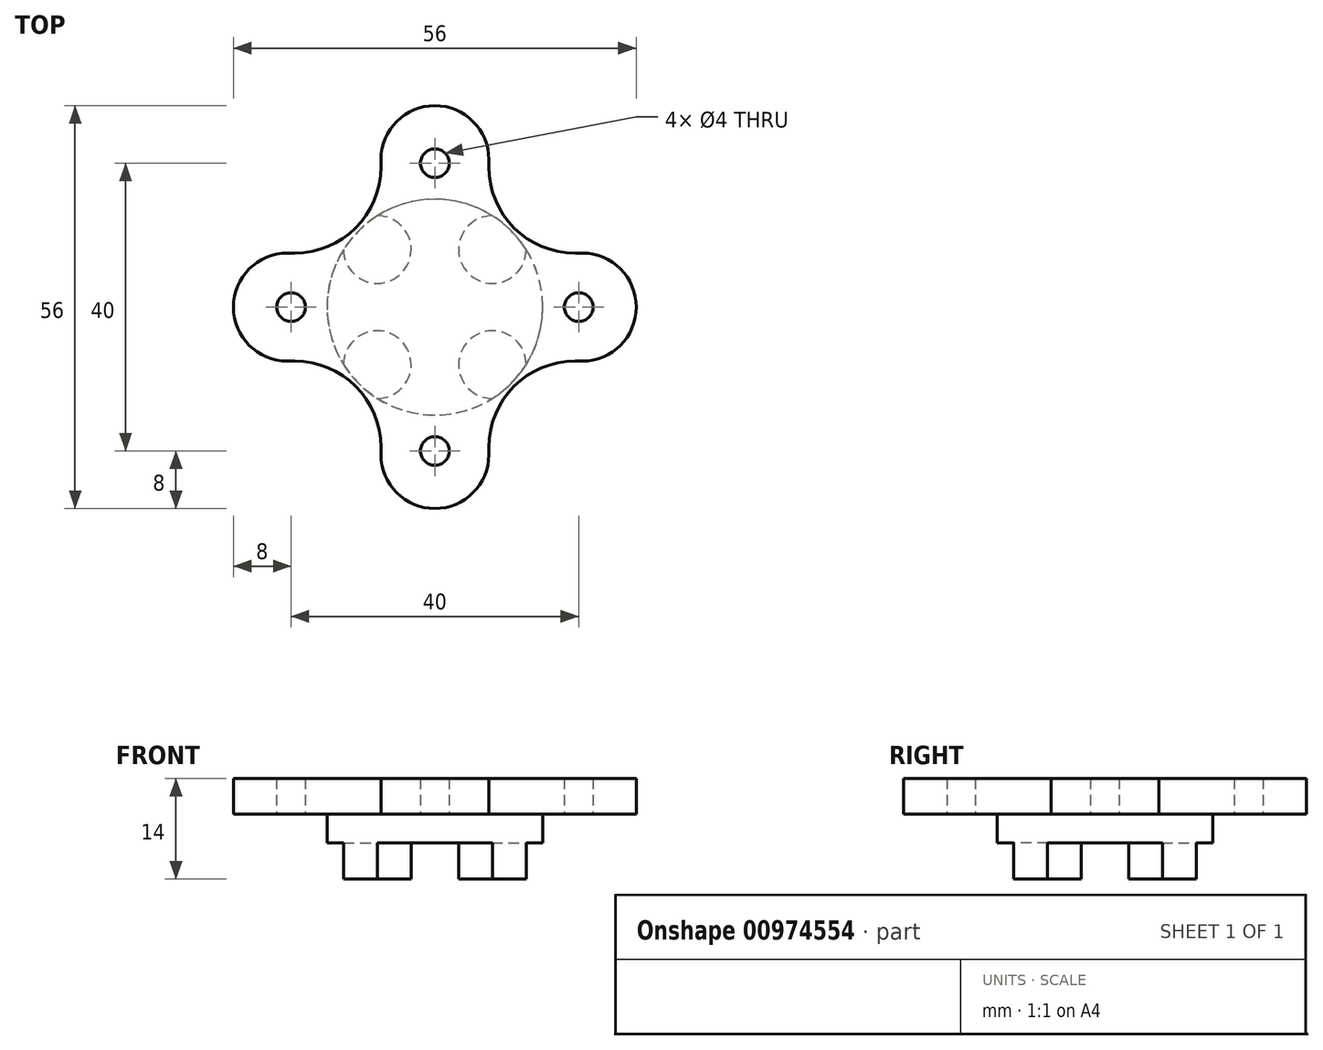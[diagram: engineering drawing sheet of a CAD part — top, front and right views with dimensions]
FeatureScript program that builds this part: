
annotation { "Feature Type Name" : "Feature", "Feature Type Description" : "" }
export const myFeature = defineFeature(function(context is Context, id is Id, definition is map)
    precondition{}
    {
        {
            var Q0;
            Q0=qCreatedBy(makeId("Top.planeOp"),FACE);
            var sketch = newSketch(context, id + "F0", { "sketchPlane" : qUnion([Q0])});
            skLineSegment(sketch, "E0", {"start": v(0, 0) * mm, "end": v(0, 52.56) * mm, "construction": true});
            skCircle(sketch, "E1", {"center": v(0, 20) * mm, "radius": 2 * mm});
            skCircle(sketch, "E2.1.0", {"center": v(-20, 0) * mm, "radius": 2 * mm});
            skCircle(sketch, "E2.2.0", {"center": v(0, -20) * mm, "radius": 2 * mm});
            skCircle(sketch, "E2.3.0", {"center": v(20, 0) * mm, "radius": 2 * mm});
            skPoint(sketch, "E2.center", {"position": v(0, 0) * mm});
            skLineSegment(sketch, "E3.bottom", {"start": v(0, 28) * mm, "end": v(0, 28) * mm});
            skLineSegment(sketch, "E3.top", {"start": v(-6.44, 0) * mm, "end": v(6.44, 0) * mm});
            skLineSegment(sketch, "E3.left", {"start": v(-7.5, 20.5) * mm, "end": v(-7.5, 19.5) * mm});
            skLineSegment(sketch, "E3.right", {"start": v(7.5, 20.5) * mm, "end": v(7.5, 19.5) * mm});
            skLineSegment(sketch, "E4.1.0", {"start": v(-28, 0) * mm, "end": v(-28, 0) * mm});
            skLineSegment(sketch, "E4.1.1", {"start": v(-20.5, -7.5) * mm, "end": v(-19.5, -7.5) * mm});
            skLineSegment(sketch, "E4.1.2", {"start": v(-20.5, 7.5) * mm, "end": v(-19.5, 7.5) * mm});
            skLineSegment(sketch, "E4.2.0", {"start": v(0, -28) * mm, "end": v(0, -28) * mm});
            skLineSegment(sketch, "E4.2.1", {"start": v(7.5, -20.5) * mm, "end": v(7.5, -19.5) * mm});
            skLineSegment(sketch, "E4.2.2", {"start": v(-7.5, -20.5) * mm, "end": v(-7.5, -19.5) * mm});
            skLineSegment(sketch, "E4.3.0", {"start": v(28, 0) * mm, "end": v(28, 0) * mm});
            skLineSegment(sketch, "E4.3.1", {"start": v(20.5, 7.5) * mm, "end": v(19.5, 7.5) * mm});
            skLineSegment(sketch, "E4.3.2", {"start": v(20.5, -7.5) * mm, "end": v(19.5, -7.5) * mm});
            skPoint(sketch, "E5.newPointA", {"position": v(1.6, 7.5) * mm});
            skPoint(sketch, "E5.newPointB", {"position": v(-7.5, -1.6) * mm});
            skArc(sketch, "E5.filletArc", {"start": v(-19.5, 7.5) * mm, "mid": v(-11.01, 11.01) * mm, "end": v(-7.5, 19.5) * mm});
            skPoint(sketch, "E6.newPointA", {"position": v(1.6, -7.5) * mm});
            skPoint(sketch, "E6.newPointB", {"position": v(-7.5, 1.6) * mm});
            skArc(sketch, "E6.filletArc", {"start": v(-7.5, -19.5) * mm, "mid": v(-11.01, -11.01) * mm, "end": v(-19.5, -7.5) * mm});
            skPoint(sketch, "E7.newPointA", {"position": v(7.5, 1.6) * mm});
            skPoint(sketch, "E7.newPointB", {"position": v(-1.6, -7.5) * mm});
            skArc(sketch, "E7.filletArc", {"start": v(19.5, -7.5) * mm, "mid": v(11.01, -11.01) * mm, "end": v(7.5, -19.5) * mm});
            skPoint(sketch, "E8.newPointA", {"position": v(-1.6, 7.5) * mm});
            skPoint(sketch, "E8.newPointB", {"position": v(7.5, -1.6) * mm});
            skArc(sketch, "E8.filletArc", {"start": v(7.5, 19.5) * mm, "mid": v(11.01, 11.01) * mm, "end": v(19.5, 7.5) * mm});
            skPoint(sketch, "E9.visualSharp", {"position": v(-7.5, 28) * mm});
            skArc(sketch, "E9.filletArc", {"start": v(0, 28) * mm, "mid": v(-5.3, 25.8) * mm, "end": v(-7.5, 20.5) * mm});
            skPoint(sketch, "E10.visualSharp", {"position": v(7.5, 28) * mm});
            skArc(sketch, "E10.filletArc", {"start": v(7.5, 20.5) * mm, "mid": v(5.3, 25.8) * mm, "end": v(0, 28) * mm});
            skPoint(sketch, "E11.visualSharp", {"position": v(-28, 7.5) * mm});
            skArc(sketch, "E11.filletArc", {"start": v(-20.5, 7.5) * mm, "mid": v(-25.8, 5.3) * mm, "end": v(-28, 0) * mm});
            skPoint(sketch, "E12.visualSharp", {"position": v(-28, -7.5) * mm});
            skArc(sketch, "E12.filletArc", {"start": v(-28, 0) * mm, "mid": v(-25.8, -5.3) * mm, "end": v(-20.5, -7.5) * mm});
            skPoint(sketch, "E13.visualSharp", {"position": v(-7.5, -28) * mm});
            skArc(sketch, "E13.filletArc", {"start": v(-7.5, -20.5) * mm, "mid": v(-5.3, -25.8) * mm, "end": v(0, -28) * mm});
            skPoint(sketch, "E14.visualSharp", {"position": v(7.5, -28) * mm});
            skArc(sketch, "E14.filletArc", {"start": v(0, -28) * mm, "mid": v(5.3, -25.8) * mm, "end": v(7.5, -20.5) * mm});
            skPoint(sketch, "E15.visualSharp", {"position": v(28, -7.5) * mm});
            skArc(sketch, "E15.filletArc", {"start": v(20.5, -7.5) * mm, "mid": v(25.8, -5.3) * mm, "end": v(28, 0) * mm});
            skPoint(sketch, "E16.visualSharp", {"position": v(28, 7.5) * mm});
            skArc(sketch, "E16.filletArc", {"start": v(28, 0) * mm, "mid": v(25.8, 5.3) * mm, "end": v(20.5, 7.5) * mm});
            skSolve(sketch);
        }
        {
            var Q0;
            Q0 = qSketchRegion(id + "F0", true);
            extrude(context, id + "F1", {"entities" : qUnion([Q0]), "depth" : 5 * mm, "offsetDistance" : 25 * mm});
        }
        {
            var Q0;
            Q0=qCreatedBy(makeId("Top.planeOp"),FACE);
            var sketch = newSketch(context, id + "F2", { "sketchPlane" : qUnion([Q0])});
            skCircle(sketch, "E17", {"center": v(0, 0) * mm, "radius": 15 * mm});
            skSolve(sketch);
        }
        {
            var Q0;
            Q0 = qSketchRegion(id + "F2", true);
            extrude(context, id + "F3", {"entities" : qUnion([Q0]), "operationType" : NewBodyOperationType.ADD, "oppositeDirection" : true, "depth" : 4 * mm, "offsetDistance" : 25 * mm});
        }
        {
            var Q0;
            Q0=makeQuery(id+"F3.opExtrude","CAP_FACE",FACE,{"disambiguationData":[OSD([sQuery(id+"F2.wireOp",EDGE,"E17")])],"isStart":false});
            var sketch = newSketch(context, id + "F4", { "sketchPlane" : qUnion([Q0])});
            skLineSegment(sketch, "E18", {"start": v(0, 14.51) * mm, "end": v(0, -15.72) * mm, "construction": true});
            skLineSegment(sketch, "E19", {"start": v(15.75, 0) * mm, "end": v(-16.53, 0) * mm, "construction": true});
            skLineSegment(sketch, "E20", {"start": v(-17.03, 8) * mm, "end": v(8, 8) * mm, "construction": true});
            skLineSegment(sketch, "E21", {"start": v(8, 8) * mm, "end": v(8, -8) * mm, "construction": true});
            skLineSegment(sketch, "E22", {"start": v(8, -8) * mm, "end": v(-8, -8) * mm, "construction": true});
            skLineSegment(sketch, "E23", {"start": v(-8, -8) * mm, "end": v(-8, 8) * mm, "construction": true});
            skArc(sketch, "E24", {"start": v(-12.7, 8) * mm, "mid": v(-4.68, 4.67) * mm, "end": v(-7.98, 12.7) * mm});
            skArc(sketch, "E25", {"start": v(7.98, 12.7) * mm, "mid": v(4.68, 4.68) * mm, "end": v(12.7, 7.98) * mm});
            skArc(sketch, "E26", {"start": v(12.7, -7.98) * mm, "mid": v(4.68, -4.68) * mm, "end": v(7.98, -12.7) * mm});
            skArc(sketch, "E27", {"start": v(-7.98, -12.7) * mm, "mid": v(-4.68, -4.68) * mm, "end": v(-12.7, -7.98) * mm});
            skArc(sketch, "E28.0", {"start": v(-7.98, 12.7) * mm, "mid": v(-10.6, 10.6) * mm, "end": v(-12.7, 7.98) * mm});
            skArc(sketch, "E29.trimOffspring", {"start": v(12.7, 7.98) * mm, "mid": v(10.6, 10.6) * mm, "end": v(7.98, 12.7) * mm});
            skArc(sketch, "E30.trimOffspring", {"start": v(7.98, -12.7) * mm, "mid": v(10.6, -10.6) * mm, "end": v(12.7, -7.98) * mm});
            skArc(sketch, "E31.trimOffspring", {"start": v(-12.7, -7.98) * mm, "mid": v(-10.6, -10.6) * mm, "end": v(-7.98, -12.7) * mm});
            skSolve(sketch);
        }
        {
            var Q0;
            Q0 = qSketchRegion(id + "F4", true);
            extrude(context, id + "F5", {"entities" : qUnion([Q0]), "operationType" : NewBodyOperationType.ADD, "depth" : 5 * mm, "offsetDistance" : 25 * mm});
        }
    });
